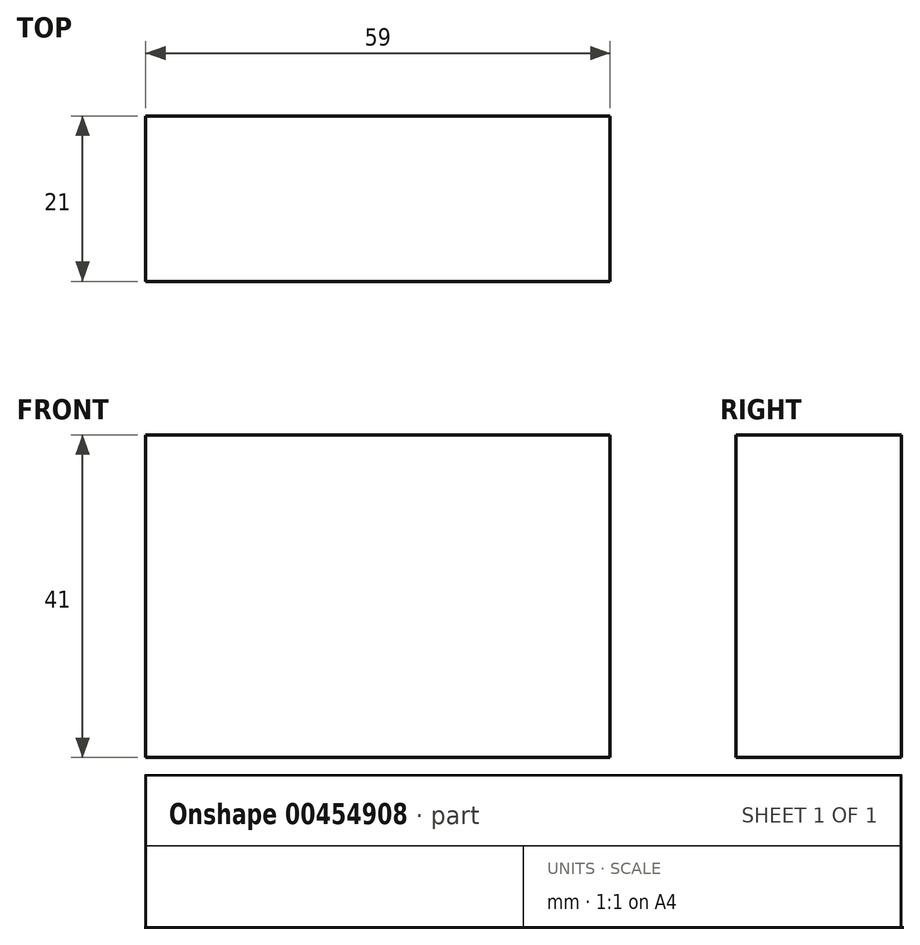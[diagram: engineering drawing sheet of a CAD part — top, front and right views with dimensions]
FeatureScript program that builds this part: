
annotation { "Feature Type Name" : "Feature", "Feature Type Description" : "" }
export const myFeature = defineFeature(function(context is Context, id is Id, definition is map)
    precondition{}
    {
        {
            var Q0;
            Q0=qCreatedBy(makeId("Front.planeOp"),FACE);
            var sketch = newSketch(context, id + "F0", { "sketchPlane" : qUnion([Q0])});
            skLineSegment(sketch, "E0.bottom", {"start": v(0, 0) * mm, "end": v(59, 0) * mm});
            skLineSegment(sketch, "E0.top", {"start": v(0, 41) * mm, "end": v(59, 41) * mm});
            skLineSegment(sketch, "E0.left", {"start": v(0, 0) * mm, "end": v(0, 41) * mm});
            skLineSegment(sketch, "E0.right", {"start": v(59, 0) * mm, "end": v(59, 41) * mm});
            skSolve(sketch);
        }
        {
            var Q0;
            Q0 = qSketchRegion(id + "F0", true);
            extrude(context, id + "F1", {"entities" : qUnion([Q0]), "depth" : 21 * mm});
        }
    });
